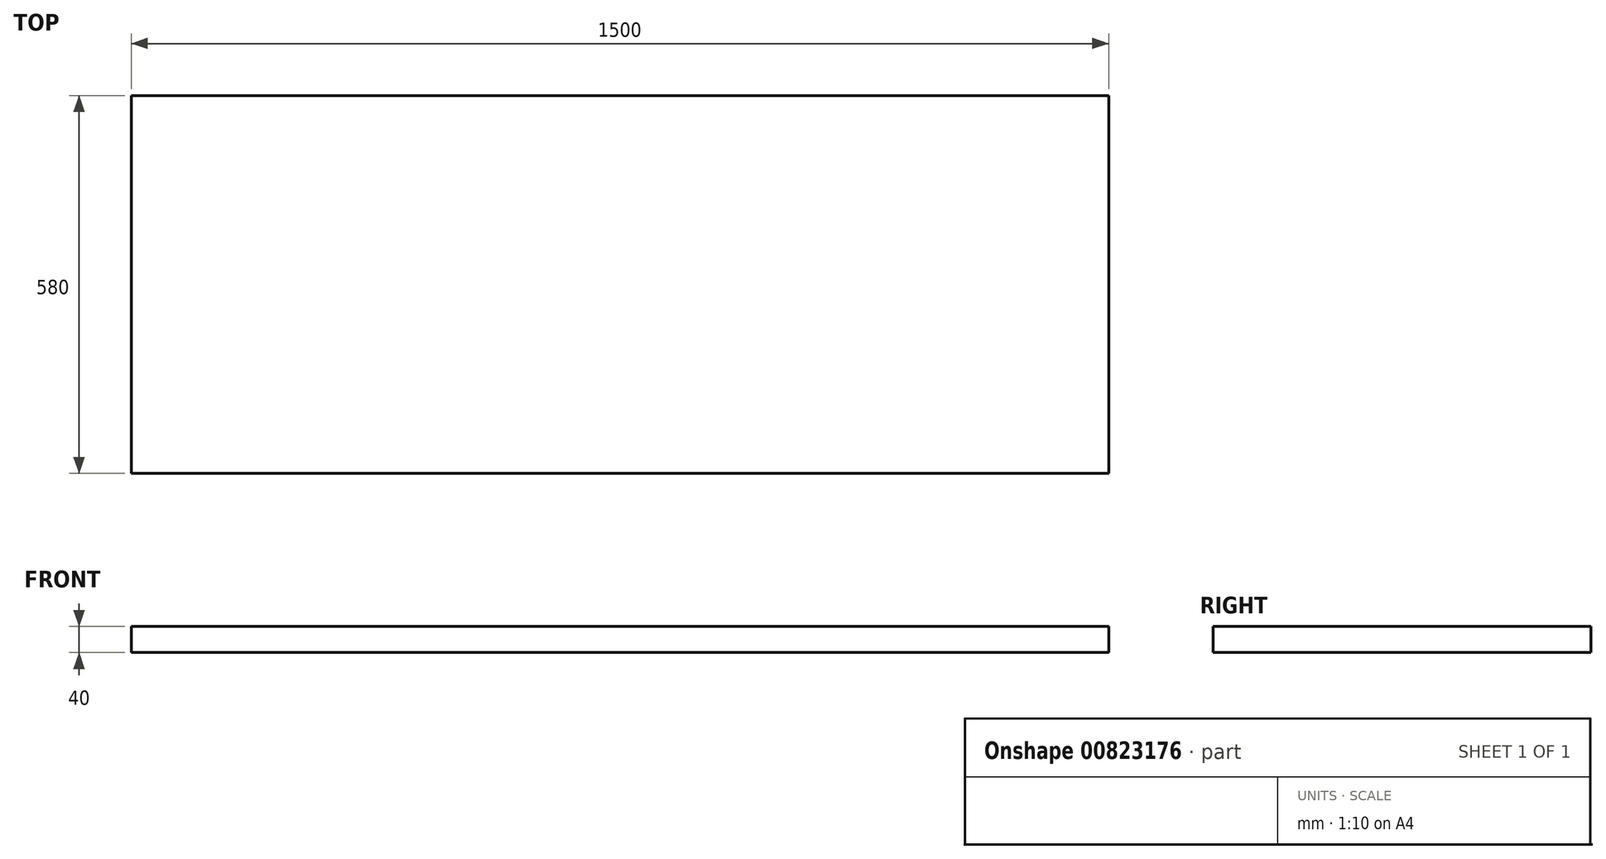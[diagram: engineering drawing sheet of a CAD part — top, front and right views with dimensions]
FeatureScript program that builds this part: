
annotation { "Feature Type Name" : "Feature", "Feature Type Description" : "" }
export const myFeature = defineFeature(function(context is Context, id is Id, definition is map)
    precondition{}
    {
        {
            var Q0;
            Q0=qCreatedBy(makeId("Top.planeOp"),FACE);
            var sketch = newSketch(context, id + "F0", { "sketchPlane" : qUnion([Q0])});
            skLineSegment(sketch, "E0.bottom", {"start": v(-1407.72, 546.06) * mm, "end": v(92.28, 546.06) * mm});
            skLineSegment(sketch, "E0.top", {"start": v(-1407.72, -33.94) * mm, "end": v(92.28, -33.94) * mm});
            skLineSegment(sketch, "E0.left", {"start": v(-1407.72, 546.06) * mm, "end": v(-1407.72, -33.94) * mm});
            skLineSegment(sketch, "E0.right", {"start": v(92.28, 546.06) * mm, "end": v(92.28, -33.94) * mm});
            skSolve(sketch);
        }
        {
            var Q0;
            Q0=makeQuery(id+"F0.imprint","IMPRINT",FACE,{"disambiguationData":[TD([[makeQuery(id+"F0.imprint","IMPRINT",EDGE,{"derivedFrom":sQuery(id+"F0.wireOp",EDGE,"E0.bottom")}),-1.0]])]});
            extrude(context, id + "F1", {"entities" : qUnion([Q0]), "depth" : 40 * mm, "offsetDistance" : 25 * mm});
        }
    });
